# Revit family: Disinfection_Shower-Whitehall-DU-1
name_source: partatom
category: Plumbing Fixtures
units: mm (PartAtom-declared; Revit-internal decimal feet)

## family parameters
Cut with Voids When Loaded = No
Host = Face
OmniClass Number = 23.45.05.14.17
OmniClass Title = Showers
Part Type = Normal
Room Calculation Point = No
Round Connector Dimension = Use Diameter
Shared = Yes

## types (1)
- DU-1
    1-Off-The-Floor, Wall Mounted = Yes
    Assembly Code = D2010710
    CL-Cylinder Lock on Access Door = No
    CW Connection = Yes
    CWFU = 3
    Cold Water Connection Diameter = 3/4"
    Control Valve Width = 11"
    Default Elevation = 0"
    Description = Wall Surface Mount Disinfection Shower
    Flow Rate = 15 GPM (57 LPM)
    HW Connection = Yes
    HWFU = 3
    Height = 39"
    Hose Material = Metal-Whitehall-Stainless Steel
    Hot Water Connection Diameter = 3/4"
    Installation Type = Wall Mounted
    Manufacturer = Whitehall Mfg.
    Max. Hot Water Temp. = 180°F (82°C)
    Maximum Operating Pressure = 125 PSI (862 kPa)
    Maximum Temperature = 110°F (43°C)
    Model = DU-1
    Mounting Height = 75 1/4"
    Product Documentation Link = https://www.whitehallmfg.com
    Product Page URL = https://www.whitehallmfg.com
    QDD-Quick Disconnect, Disinfectant Sprayer = No
    QDS-Quick Disconnect, Stainless Steel Filler Hose = No
    QPD Quick Disconnect, Patient Shower = No
    SSF-Stainless Steel Filler Hose, 120” (3048) = No
    Showerhead Material = Stainless Steel-Whitehall-White
    TSF-Tub Filler Spout = No
    URL = https://www.whitehallmfg.com
    Vent Connection = No
    WFU = 4
    Wall Mounted Console Material = Stainless Steel-Whitehall-Satin
    Waste Connection = No
    Width = 15"
    XLD-Extra Long Hose, Disinfectant Sprayer = No
    XLP-Extra Long Hose, Patient Shower = No

## geometry (parser evidence)
native form markers: Sweep x3
no freeform markers — native parametric forms only
